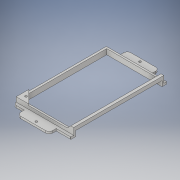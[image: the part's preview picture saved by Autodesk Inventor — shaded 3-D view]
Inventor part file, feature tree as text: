
AUTODESK INVENTOR PART (.ipt)
format: ipt  version: 2019 (Build 230136000, 136)  size: 285,696 bytes
history: native  units: mm
features: extrude x10, sketch x9, projected_geometry x9, plane x2, other x1, hole x1
ambient origin geometry x8: Origin, YZ Plane, XZ Plane, XY Plane, X Axis, Y Axis, Z Axis, Center Point
bodies: Volumenkörper1 (feature_tree)
feature tree (32):
  extrude  "Extrusion1"  Depth=121.0mm
  sketch  "Skizze2"  dims[d2=3.0mm d3=7.5mm d4=0.0mm]
  extrude  "Extrusion2"  Depth=7.5mm TaperAngle=0.0deg
  extrude  "Extrusion3"  Depth=4.5mm
  other  "Arbeitsachse1"
  sketch  "Skizze4"  dims[d7=18.0mm d9=18.0mm]
  extrude  "Extrusion4"  Depth=18.0mm
  extrude  "Extrusion5"  Depth=3.0mm
  hole  "Bohrung1"  [1 undecoded]
  extrude  "Extrusion8"  Depth=4.0mm
  extrude  "Extrusion9"  Depth=4.0mm
  extrude  "Extrusion10"  Depth=4.0mm
  extrude  "Extrusion11"  Depth=4.0mm
  extrude  "Extrusion12"  Depth=3.0mm TaperAngle=0.0deg
  sketch  "Skizze1"  dims[d0=78.0mm d1=121.0mm]
  sketch  "Skizze3"  dims[d5=4.5mm d6=3.5mm]
  plane  "Arbeitsebene1"
  plane  "Arbeitsebene2"
  projected_geometry  "Projizierte Kontur1"
  sketch  "Skizze6"  dims[d10=2.0mm d11=0.0mm d12=3.0mm]
  projected_geometry  "Projizierte Kontur3"
  projected_geometry  "Projizierte Kontur4"
  projected_geometry  "Projizierte Kontur5"
  sketch  "Skizze7"  dims[d13=3.0mm d14=0.0mm d20=155.0mm]
  projected_geometry  "Projizierte Kontur6"
  projected_geometry  "Projizierte Kontur7"
  sketch  "Skizze8"  dims[d21=45.0mm d22=4.0mm]
  projected_geometry  "Projizierte Kontur8"
  sketch  "Skizze9"  dims[d23=135.0mm d24=4.0mm]
  projected_geometry  "Projizierte Kontur9"
  sketch  "Skizze10"  dims[d25=4.0mm d26=4.0mm d27=4.0mm d28=3.0mm d29=0.0mm d30=5.0mm d31=3.0mm d32=0.0mm d33=5.5mm d34=3.0mm d35=6.0mm d36=4.0mm d37=2.0mm d38=90.0deg d39=10.0mm d40=0.0mm d46=10.0mm d47=0.0mm d48=4.0mm d49=5.0mm d50=0.0mm d51=45.0deg d52=5.0mm d53=0.0mm d54=5.0mm d55=0.0mm d56=0.5mm d57=0.5mm d58=10.0mm d59=0.0mm]
  projected_geometry  "Projizierte Kontur10"
note: 1 required parameter value undecoded (feature->parameter linkage not recoverable at this tier; creation-order binding heuristic only, values carry confidence <= 0.55)
